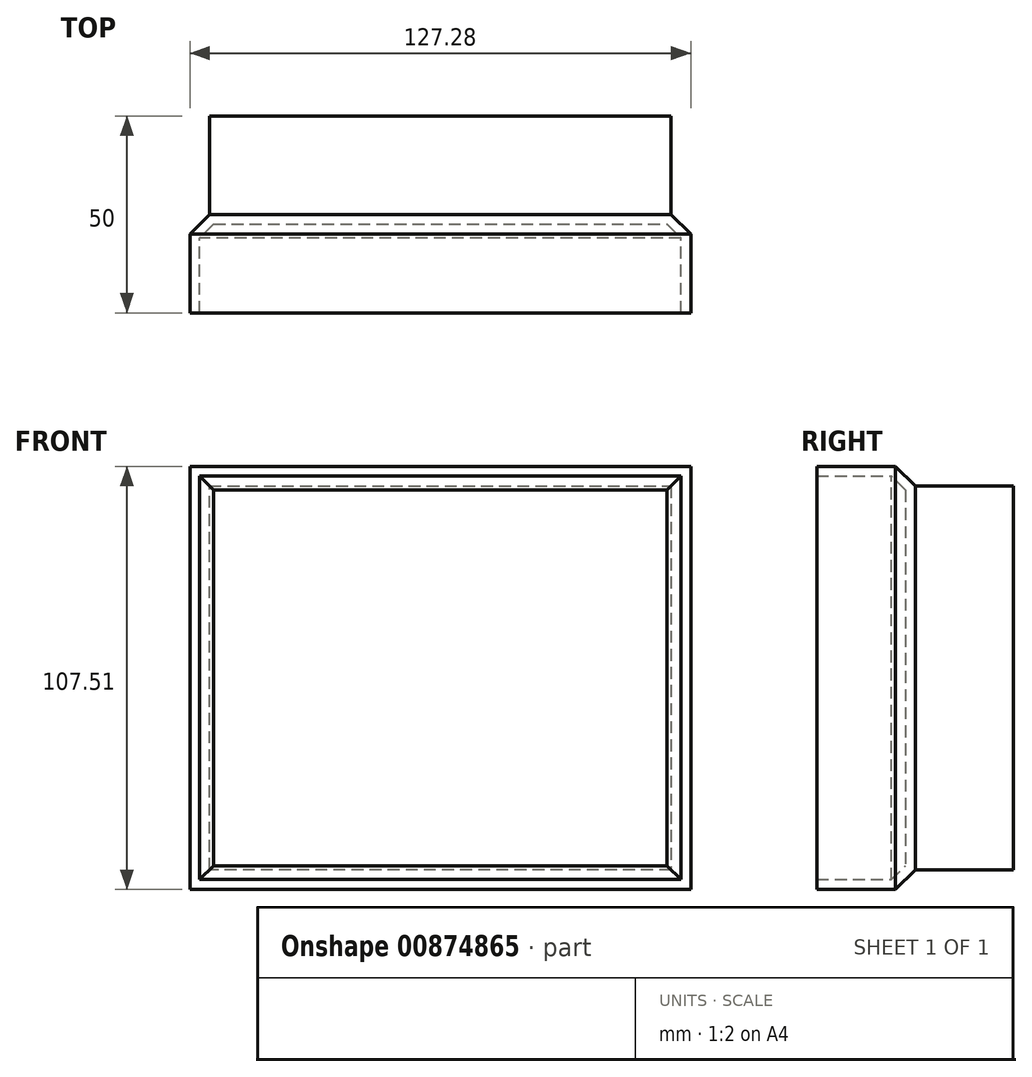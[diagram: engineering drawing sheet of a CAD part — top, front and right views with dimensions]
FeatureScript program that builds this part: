
annotation { "Feature Type Name" : "Feature", "Feature Type Description" : "" }
export const myFeature = defineFeature(function(context is Context, id is Id, definition is map)
    precondition{}
    {
        {
            var Q0;
            Q0=qCreatedBy(makeId("Front.planeOp"),FACE);
            var sketch = newSketch(context, id + "F0", { "sketchPlane" : qUnion([Q0])});
            skLineSegment(sketch, "E0.bottom", {"start": v(-65.9, 44.05) * mm, "end": v(61.38, 44.05) * mm});
            skLineSegment(sketch, "E0.top", {"start": v(-65.9, -63.46) * mm, "end": v(61.38, -63.46) * mm});
            skLineSegment(sketch, "E0.left", {"start": v(-65.9, 44.05) * mm, "end": v(-65.9, -63.46) * mm});
            skLineSegment(sketch, "E0.right", {"start": v(61.38, 44.05) * mm, "end": v(61.38, -63.46) * mm});
            skSolve(sketch);
        }
        {
            var Q0;
            Q0=makeQuery(id+"F0.imprint","IMPRINT",FACE,{"disambiguationData":[TD([[makeQuery(id+"F0.imprint","IMPRINT",EDGE,{"derivedFrom":sQuery(id+"F0.wireOp",EDGE,"E0.bottom")}),-1.0]])]});
            extrude(context, id + "F1", {"entities" : qUnion([Q0]), "depth" : 25 * mm, "offsetDistance" : 25 * mm});
        }
        {
            var Q0;
            Q0=makeQuery(id+"F1.opExtrude","CAP_EDGE",EDGE,{"disambiguationData":[OSD([sQuery(id+"F0.wireOp",EDGE,"E0.right")])],"isStart":true});
            var Q1;
            Q1=makeQuery(id+"F1.opExtrude","CAP_EDGE",EDGE,{"disambiguationData":[OSD([sQuery(id+"F0.wireOp",EDGE,"E0.top")])],"isStart":true});
            var Q2;
            Q2=makeQuery(id+"F1.opExtrude","CAP_EDGE",EDGE,{"disambiguationData":[OSD([sQuery(id+"F0.wireOp",EDGE,"E0.left")])],"isStart":true});
            var Q3;
            Q3=makeQuery(id+"F1.opExtrude","CAP_EDGE",EDGE,{"disambiguationData":[OSD([sQuery(id+"F0.wireOp",EDGE,"E0.bottom")])],"isStart":true});
            chamfer(context, id + "F2", {"entities" : qUnion([Q0, Q1, Q2, Q3]), "width" : 5 * mm, "tangentPropagation" : true});
        }
        {
            var Q0;
            Q0=makeQuery(id+"F1.opExtrude","CAP_FACE",FACE,{"disambiguationData":[OSD([sQuery(id+"F0.wireOp",EDGE,"E0.bottom"),sQuery(id+"F0.wireOp",EDGE,"E0.top"),sQuery(id+"F0.wireOp",EDGE,"E0.left"),sQuery(id+"F0.wireOp",EDGE,"E0.right")])],"isStart":false});
            shell(context, id + "F3", {"entities" : qUnion([Q0]), "thickness" : 2.5 * mm});
        }
        {
            var Q0;
            Q0=makeQuery(id+"F1.opExtrude","CAP_FACE",FACE,{"disambiguationData":[OSD([sQuery(id+"F0.wireOp",EDGE,"E0.bottom"),sQuery(id+"F0.wireOp",EDGE,"E0.top"),sQuery(id+"F0.wireOp",EDGE,"E0.left"),sQuery(id+"F0.wireOp",EDGE,"E0.right")])],"isStart":true});
            var sketch = newSketch(context, id + "F4", { "sketchPlane" : qUnion([Q0])});
            skSolve(sketch);
        }
        {
            var Q0;
            {var subQ0=sQuery(id+"F0.wireOp",EDGE,"E0.right");var subQ1=sQuery(id+"F0.wireOp",EDGE,"E0.left");var subQ2=sQuery(id+"F0.wireOp",EDGE,"E0.top");var subQ3=sQuery(id+"F0.wireOp",EDGE,"E0.bottom");var subQ4=makeQuery(id+"F1.opExtrude","CAP_FACE",FACE,{"disambiguationData":[OSD([subQ3,subQ2,subQ1,subQ0])],"isStart":true});Q0=makeQuery(id+"F4.imprint","IMPRINT",FACE,{"disambiguationData":[TD([[makeQuery(id+"F4.imprint","IMPRINT",EDGE,{"derivedFrom":makeQuery(id+"F2.opChamfer","BLEND_EDGE",EDGE,{"blendedFrom":[makeQuery(id+"F1.opExtrude","CAP_EDGE",EDGE,{"disambiguationData":[OSD([subQ3])],"isStart":true}),subQ4],"blendedInto":[subQ4]})}),1.0]])]});}
            extrude(context, id + "F5", {"entities" : qUnion([Q0]), "operationType" : NewBodyOperationType.ADD, "depth" : 25 * mm, "offsetDistance" : 25 * mm});
        }
    });
